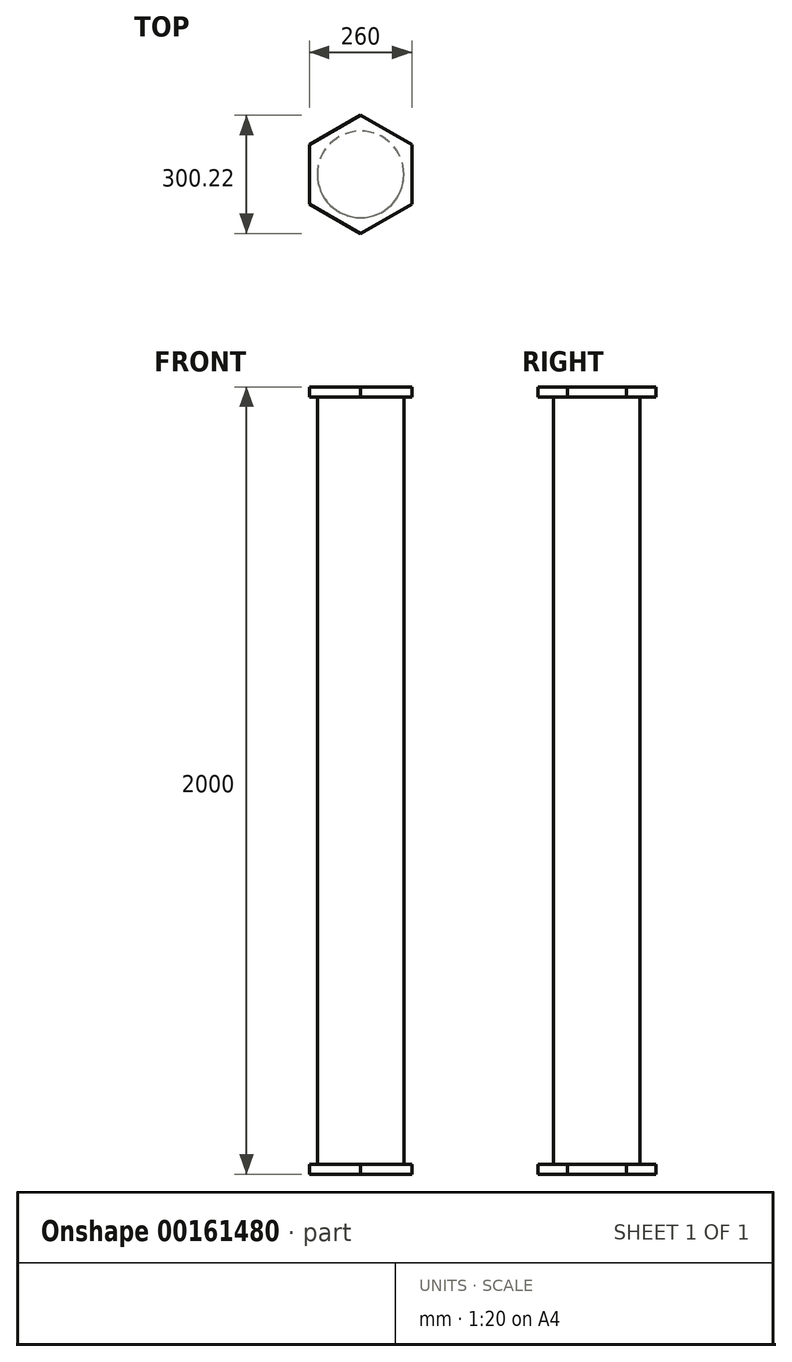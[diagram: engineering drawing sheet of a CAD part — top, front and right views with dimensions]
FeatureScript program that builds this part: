
annotation { "Feature Type Name" : "Feature", "Feature Type Description" : "" }
export const myFeature = defineFeature(function(context is Context, id is Id, definition is map)
    precondition{}
    {
        {
            var Q0;
            Q0=qCreatedBy(makeId("Top.planeOp"),FACE);
            var sketch = newSketch(context, id + "F0", { "sketchPlane" : qUnion([Q0])});
            skCircle(sketch, "E0", {"center": v(0, 0) * mm, "radius": 110 * mm});
            skSolve(sketch);
        }
        {
            var Q0;
            Q0=makeQuery(id+"F0.imprint","IMPRINT",FACE,{"disambiguationData":[TD([[makeQuery(id+"F0.imprint","IMPRINT",EDGE,{"derivedFrom":sQuery(id+"F0.wireOp",EDGE,"E0")}),1.0]])]});
            extrude(context, id + "F1", {"entities" : qUnion([Q0]), "depth" : 2000 * mm});
        }
        {
            var Q0;
            Q0=makeQuery(id+"F1.opExtrude","CAP_FACE",FACE,{"disambiguationData":[OSD([sQuery(id+"F0.wireOp",EDGE,"E0")])],"isStart":false});
            var sketch = newSketch(context, id + "F2", { "sketchPlane" : qUnion([Q0])});
            skCircle(sketch, "E1.cCircle", {"center": v(0, 0) * mm, "radius": 130 * mm, "construction": true});
            skLineSegment(sketch, "E1.0", {"start": v(130, 75.06) * mm, "end": v(130, -75.06) * mm});
            skLineSegment(sketch, "E1.1", {"start": v(130, -75.06) * mm, "end": v(0, -150.11) * mm});
            skLineSegment(sketch, "E1.2", {"start": v(0, -150.11) * mm, "end": v(-130, -75.06) * mm});
            skLineSegment(sketch, "E1.3", {"start": v(-130, -75.06) * mm, "end": v(-130, 75.06) * mm});
            skLineSegment(sketch, "E1.4", {"start": v(-130, 75.06) * mm, "end": v(0, 150.11) * mm});
            skLineSegment(sketch, "E1.5", {"start": v(0, 150.11) * mm, "end": v(130, 75.06) * mm});
            skPoint(sketch, "E1.0.midPoint", {"position": v(130, 0) * mm});
            skSolve(sketch);
        }
        {
            var Q0;
            Q0 = qSketchRegion(id + "F2", true);
            extrude(context, id + "F3", {"entities" : qUnion([Q0]), "operationType" : NewBodyOperationType.ADD, "oppositeDirection" : true, "depth" : 25 * mm});
        }
        {
            var Q0;
            Q0=makeQuery(id+"F1.opExtrude","CAP_FACE",FACE,{"disambiguationData":[OSD([sQuery(id+"F0.wireOp",EDGE,"E0")])],"isStart":true});
            var sketch = newSketch(context, id + "F4", { "sketchPlane" : qUnion([Q0])});
            skCircle(sketch, "E2.cCircle", {"center": v(0, 0) * mm, "radius": 130 * mm, "construction": true});
            skLineSegment(sketch, "E2.0", {"start": v(130, 75.06) * mm, "end": v(130, -75.06) * mm});
            skLineSegment(sketch, "E2.1", {"start": v(130, -75.06) * mm, "end": v(0, -150.11) * mm});
            skLineSegment(sketch, "E2.2", {"start": v(0, -150.11) * mm, "end": v(-130, -75.06) * mm});
            skLineSegment(sketch, "E2.3", {"start": v(-130, -75.06) * mm, "end": v(-130, 75.06) * mm});
            skLineSegment(sketch, "E2.4", {"start": v(-130, 75.06) * mm, "end": v(0, 150.11) * mm});
            skLineSegment(sketch, "E2.5", {"start": v(0, 150.11) * mm, "end": v(130, 75.06) * mm});
            skPoint(sketch, "E2.0.midPoint", {"position": v(130, 0) * mm});
            skSolve(sketch);
        }
        {
            var Q0;
            Q0 = qSketchRegion(id + "F4", true);
            extrude(context, id + "F5", {"entities" : qUnion([Q0]), "operationType" : NewBodyOperationType.ADD, "oppositeDirection" : true, "depth" : 25 * mm});
        }
    });
